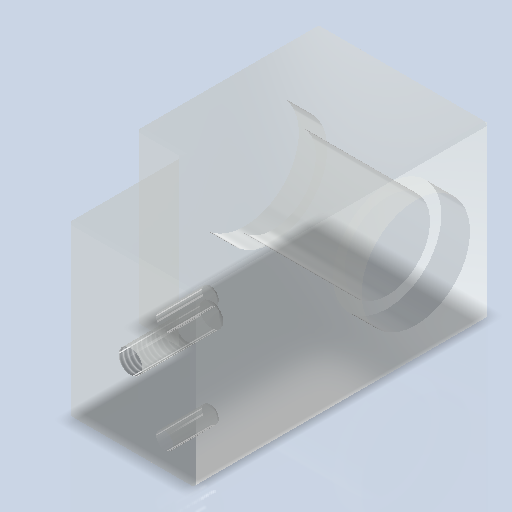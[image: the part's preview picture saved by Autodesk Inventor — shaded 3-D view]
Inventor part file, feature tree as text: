
AUTODESK INVENTOR PART (.ipt)
format: ipt  version: 2024.2 (Build 282272000, 272)  size: 277,504 bytes
history: native  units: mm
features: sketch x6, hole x5, extrude x1, chamfer x1
ambient origin geometry x8: Origin, YZ Plane, XZ Plane, XY Plane, X Axis, Y Axis, Z Axis, Center Point
bodies: Volumenkörper1 (feature_tree)
feature tree (13):
  extrude  "Extrusion1"  Depth=20.0mm
  hole  "Bohrung1"  [1 undecoded]
  hole  "Bohrung2"  [1 undecoded]
  hole  "Bohrung3"  [1 undecoded]
  hole  "Bohrung4"  [1 undecoded]
  hole  "Bohrung5"  [1 undecoded]
  chamfer  "Fasen1"  Distance=14.0mm
  sketch  "Skizze1"  dims[d0=22.0mm d1=20.0mm]
  sketch  "Skizze2"  dims[d2=52.0mm d4=30.0mm]
  sketch  "Skizze3"  dims[d5=30.0mm d6=0.0mm]
  sketch  "Skizze4"  dims[d7=15.0mm d8=6.0mm d9=19.0mm d10=5.0mm d11=90.0deg d12=17.0mm d13=0.0mm d14=39.0mm]
  sketch  "Skizze5"  dims[d15=15.0mm d16=6.0mm d17=19.0mm d18=5.0mm d19=90.0deg d20=17.0mm d21=0.0mm d22=39.0mm]
  sketch  "Skizze6"  dims[d23=3.0mm d24=6.0mm d25=19.0mm d26=5.0mm d27=90.0deg d28=8.0mm d29=20.594885mm d30=5.0mm d31=5.0mm d32=4.134mm d33=10.0mm d34=4.0mm d35=2.0mm d36=90.0deg d37=14.2mm d38=20.594885mm d39=14.0mm d40=11.0mm d41=3.0mm d42=10.0mm d43=4.0mm d44=2.0mm d45=90.0deg d46=8.0mm d47=20.594885mm d49=5.0mm d50=23.0mm d51=0.5mm d52=2.0mm d53=45.0deg]
note: 5 required parameter values undecoded (feature->parameter linkage not recoverable at this tier; creation-order binding heuristic only, values carry confidence <= 0.55)
